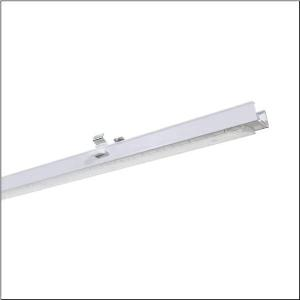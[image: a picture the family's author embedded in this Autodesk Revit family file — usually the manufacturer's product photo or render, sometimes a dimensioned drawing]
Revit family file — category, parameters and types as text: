
# Revit family: trunking_flex_31_51re14mb4cb
name_source: partatom
category: Lighting Fixtures
units: mm (PartAtom-declared; Revit-internal decimal feet)

## family parameters
Cut with Voids When Loaded = No
Host = Face
Light Source = No
Part Type = Normal
Room Calculation Point = No
Round Connector Dimension = Use Diameter
Shared = No

## types (1)
- --- (1 x LED, 11500 lm, 66 W, 4000K)
    Apparent Load = 66 VA
    CIE Flux Codes = 72 92 98 99 100
    Color Rendering = 80
    Color Temperature = 4000K
    Default Elevation = 1800 mm
    Description = Trunking Flex 31, luminaire insert, of extruded aluminium section, coated, traffic white (RAL 9016), length: 1.472mm, width: 91mm, height: 53mm, LED rated luminous flux: 11.500lm, light colour: 840, control gear: ON/OFF Multilumen, with system connector: socket, mains connection: 220..240V, AC, 50/60Hz, rated input power: 66W, connected load according to luminous flux setting (19/24/32/37/47/52/60/66W), luminous flux adjustable on luminaire in eight steps (3450/4380/5800/6700/8350/9200/10500/11500lm ), primary light control with lens, of plastic, primary optical cover: cover, of PMMA, light emission: direct distribution, primary light characteristic: asymmetric, protection rating (complete): IP20, insulation class (complete): insulation class I (protective earthing), certification: CE, UKCA, impact resistance: IK02, permissible ambient temperature for indoor applications: -20..+40°C, packaging unit: 1 piece
    Height = 58 mm
    Lamp = 1 x LED
    Lamp Light Flux = 11500 lm
    Lamp Power = 66 W
    Lamp count = 1
    Length = 1472 mm
    Luminous efficacy = 174 lm/W
    Manufacturer = Siteco
    ModVariant = No
    Model = 51RE14MB4CB
    Mounting Place = Ceiling
    Mounting Type = Pendant
    Number of Poles = 1
    OnlyDefault = Yes
    Power Factor = 1
    Product Name = Trunking Flex 31
    Product group = luminaire insert
    ProductGroupID = 901
    Protection Class = Protection class I
    Protection Degree = IP 20
    RLX_Detail_Level = 1
    RLX_Emergency_Light_Flux = 0 lm
    RLX_Emergency_Type = 0
    RLX_Emergency_Type_DB = No
    RlxData = <blob elided: 21733 chars, md5=2162af5a>
    Socket = socket
    Standby Power = 0 W
    System Light Flux = 11500 lm
    System Power = 66 W
    Type Comments = factory setting: luminous flux: 100 % | (ON | ON | ON)
    Type Image = l_1266702.jpg
    URL = http://relux.com
    VarID = @adj_001367
    Voltage = 0 V
    Weight = 0.00 kg
    Width = 65 mm

## geometry (parser evidence)
native form markers: Blend x4, Sweep x11
no freeform markers — native parametric forms only
